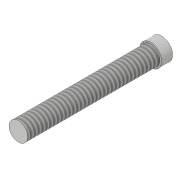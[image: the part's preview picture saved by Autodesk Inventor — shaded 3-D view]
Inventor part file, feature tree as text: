
AUTODESK INVENTOR PART (.ipt)
format: ipt  version: 2019 (Build 230136000, 136)  size: 87,040 bytes
history: native  units: in
note: dims shown in document units (in); Inventor stores cm internally (conversion verified against a paired STEP export)
features: extrude x2, sketch x2, thread x1
ambient origin geometry x8: Origin, YZ Plane, XZ Plane, XY Plane, X Axis, Y Axis, Z Axis, Center Point
bodies: Solid1 (feature_tree)
feature tree (5):
  extrude  "Extrusion1"  Depth=0.0394in TaperAngle=0.0deg
  extrude  "Extrusion2"  Depth=0.4724in TaperAngle=0.0deg
  thread  "Thread1"  [1 undecoded]
  sketch  "Sketch1"  dims[d0=0.0787in d1=0.0394in d2=0.0in]
  sketch  "Sketch2"  dims[d3=0.0669in d4=0.4724in d5=0.0in d6=0.3937in d7=0.0in]
note: 1 required parameter value undecoded (feature->parameter linkage not recoverable at this tier; creation-order binding heuristic only, values carry confidence <= 0.55)
